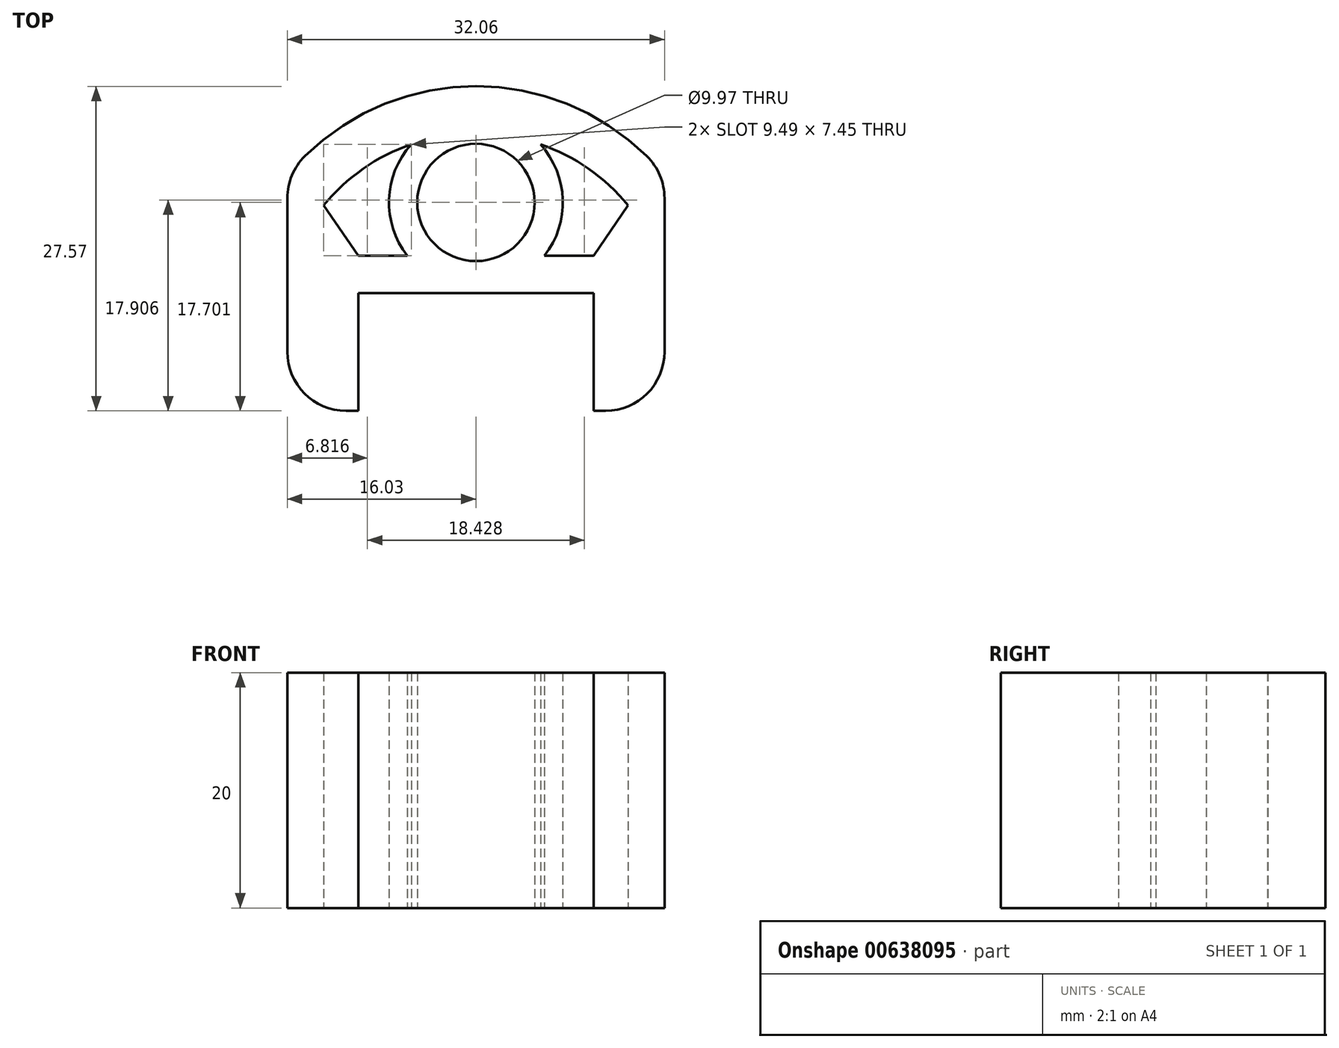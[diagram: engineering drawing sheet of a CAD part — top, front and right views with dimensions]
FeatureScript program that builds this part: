
annotation { "Feature Type Name" : "Feature", "Feature Type Description" : "" }
export const myFeature = defineFeature(function(context is Context, id is Id, definition is map)
    precondition{}
    {
        {
            var Q0;
            Q0=qCreatedBy(makeId("Top.planeOp"),FACE);
            var sketch = newSketch(context, id + "F0", { "sketchPlane" : qUnion([Q0])});
            skLineSegment(sketch, "E0.bottom", {"start": v(10, -10) * mm, "end": v(-10, -10) * mm});
            skLineSegment(sketch, "E0.top", {"start": v(10, 10) * mm, "end": v(-10, 10) * mm});
            skLineSegment(sketch, "E0.left", {"start": v(10, -10) * mm, "end": v(10, 10) * mm});
            skLineSegment(sketch, "E0.right", {"start": v(-10, -10) * mm, "end": v(-10, 10) * mm});
            skPoint(sketch, "E0.middle", {"position": v(0, 0) * mm});
            skLineSegment(sketch, "E1.bottom", {"start": v(11.03, 0) * mm, "end": v(-11.03, 0) * mm});
            skLineSegment(sketch, "E1.left", {"start": v(16.03, 5) * mm, "end": v(16.03, 18.07) * mm});
            skLineSegment(sketch, "E1.right", {"start": v(-16.03, 5) * mm, "end": v(-16.03, 18.07) * mm});
            skPoint(sketch, "E1.middle", {"position": v(0, 10) * mm});
            skPoint(sketch, "E1.cornerSnap0", {"position": v(10, 0) * mm});
            skArc(sketch, "E2", {"start": v(14.53, 21.64) * mm, "mid": v(0, 27.57) * mm, "end": v(-14.53, 21.64) * mm});
            skCircle(sketch, "E3", {"center": v(0, 17.7) * mm, "radius": 4.99 * mm});
            skPoint(sketch, "E3.centerSnap0", {"position": v(0, 20) * mm});
            skCircle(sketch, "E4", {"center": v(0, 17.7) * mm, "radius": 7.39 * mm});
            skArc(sketch, "E5.0", {"start": v(12.94, 17.46) * mm, "mid": v(0, 23.57) * mm, "end": v(-12.94, 17.46) * mm});
            skLineSegment(sketch, "E6", {"start": v(-12.94, 17.46) * mm, "end": v(-10, 13.16) * mm});
            skLineSegment(sketch, "E7", {"start": v(-10, 13.16) * mm, "end": v(10, 13.16) * mm});
            skLineSegment(sketch, "E8", {"start": v(10, 13.16) * mm, "end": v(12.94, 17.46) * mm});
            skPoint(sketch, "E9.visualSharp", {"position": v(-16.03, 0) * mm});
            skArc(sketch, "E9.filletArc", {"start": v(-16.03, 5) * mm, "mid": v(-14.57, 1.46) * mm, "end": v(-11.03, 0) * mm});
            skPoint(sketch, "E10.visualSharp", {"position": v(16.03, 0) * mm});
            skArc(sketch, "E10.filletArc", {"start": v(11.03, 0) * mm, "mid": v(14.57, 1.46) * mm, "end": v(16.03, 5) * mm});
            skPoint(sketch, "E11.visualSharp", {"position": v(-16.03, 20) * mm});
            skArc(sketch, "E11.filletArc", {"start": v(-14.53, 21.64) * mm, "mid": v(-15.64, 20) * mm, "end": v(-16.03, 18.07) * mm});
            skPoint(sketch, "E12.visualSharp", {"position": v(16.03, 20) * mm});
            skArc(sketch, "E12.filletArc", {"start": v(16.03, 18.07) * mm, "mid": v(15.64, 20) * mm, "end": v(14.53, 21.64) * mm});
            skSolve(sketch);
        }
        {
            var Q0;
            {var subQ4=sQuery(id+"F0.wireOp",EDGE,"E0.top");Q0=makeQuery(id+"F0.imprint","IMPRINT",FACE,{"disambiguationData":[TD([[makeQuery(id+"F0.imprint","IMPRINT",EDGE,{"derivedFrom":subQ4}),-1.0]])]});}
            var Q1;
            {var subQ4=sQuery(id+"F0.wireOp",EDGE,"E7");var subQ7=sQuery(id+"F0.wireOp",EDGE,"E3");var subQ8=makeQuery(id+"F0.imprint","INTERSECT",VERTEX,{"disambiguationData":[OD(0.0)],"derivedFrom":[subQ7,subQ4]});Q1=makeQuery(id+"F0.imprint","IMPRINT",FACE,{"disambiguationData":[TD([[makeQuery(id+"F0.imprint","IMPRINT",EDGE,{"disambiguationData":[TD([[subQ8,1.0]])],"derivedFrom":subQ7}),-1.0]])]});}
            var Q2;
            {var subQ0=sQuery(id+"F0.wireOp",EDGE,"E5.0");var subQ1=sQuery(id+"F0.wireOp",EDGE,"E4");var subQ2=makeQuery(id+"F0.imprint","INTERSECT",VERTEX,{"disambiguationData":[OD(0.0)],"derivedFrom":[subQ1,subQ0]});Q2=makeQuery(id+"F0.imprint","IMPRINT",FACE,{"disambiguationData":[TD([[makeQuery(id+"F0.imprint","IMPRINT",EDGE,{"disambiguationData":[TD([[subQ2,1.0]])],"derivedFrom":subQ1}),1.0]])]});}
            var Q3;
            {var subQ0=sQuery(id+"F0.wireOp",EDGE,"E7");var subQ1=sQuery(id+"F0.wireOp",EDGE,"E3");var subQ2=makeQuery(id+"F0.imprint","INTERSECT",VERTEX,{"disambiguationData":[OD(0.0)],"derivedFrom":[subQ1,subQ0]});Q3=makeQuery(id+"F0.imprint","IMPRINT",FACE,{"disambiguationData":[TD([[makeQuery(id+"F0.imprint","IMPRINT",EDGE,{"disambiguationData":[TD([[subQ2,-1.0]])],"derivedFrom":subQ1}),-1.0]])]});}
            extrude(context, id + "F1", {"entities" : qUnion([Q0, Q1, Q2, Q3]), "depth" : 20 * mm});
        }
    });
